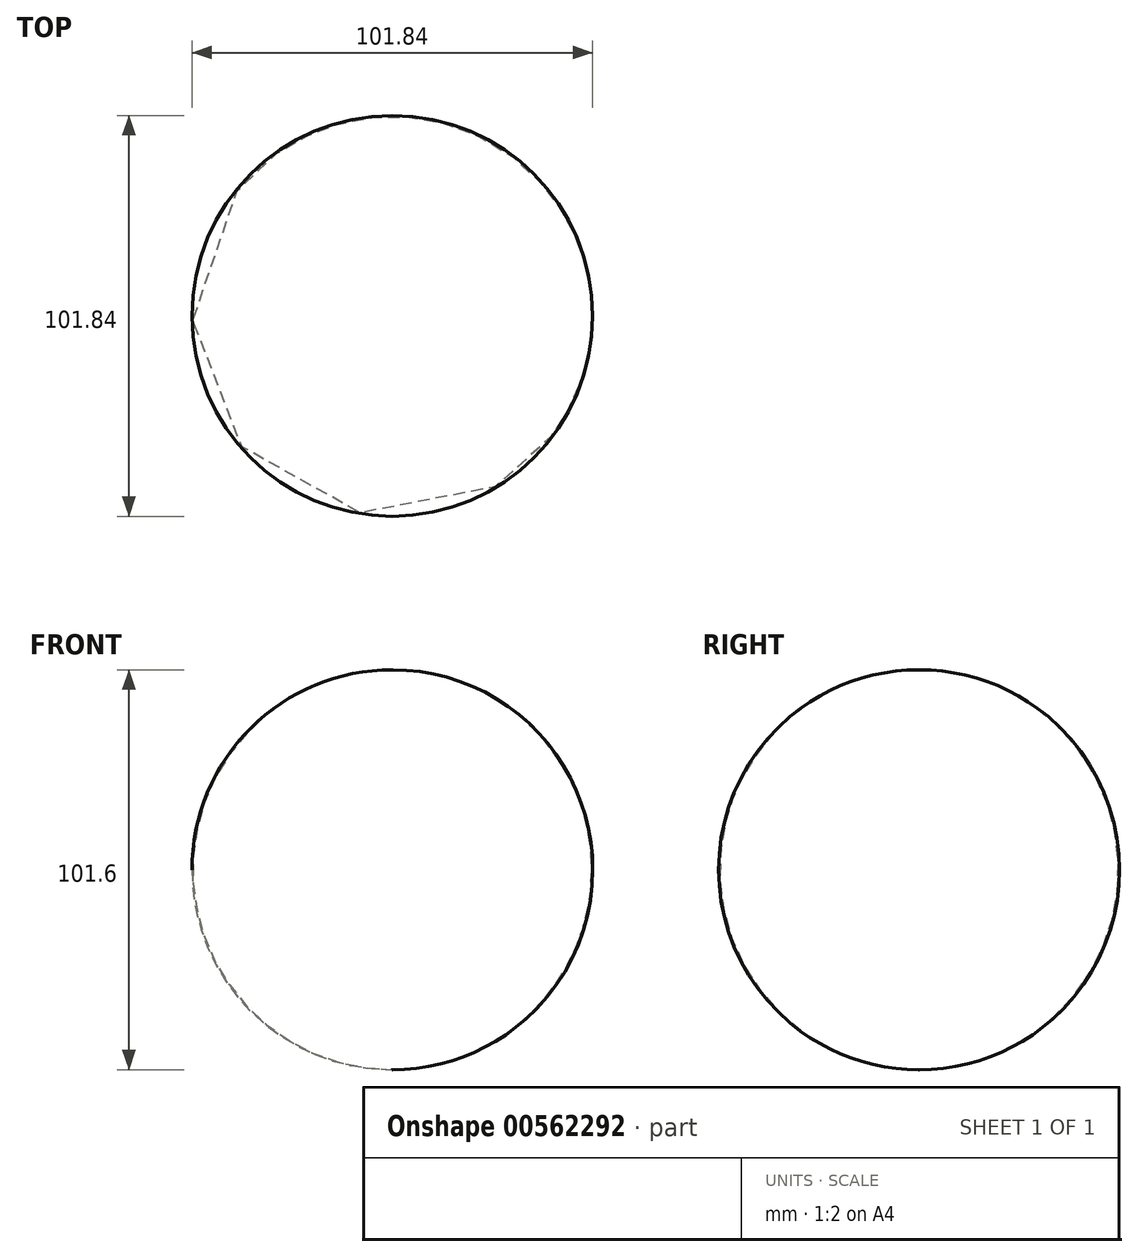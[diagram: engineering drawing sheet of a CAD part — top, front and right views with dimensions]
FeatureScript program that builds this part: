
annotation { "Feature Type Name" : "Feature", "Feature Type Description" : "" }
export const myFeature = defineFeature(function(context is Context, id is Id, definition is map)
    precondition{}
    {
        {
            var Q0;
            Q0=qCreatedBy(makeId("Front.planeOp"),FACE);
            var sketch = newSketch(context, id + "F0", { "sketchPlane" : qUnion([Q0])});
            skLineSegment(sketch, "E0", {"start": v(0, -48.96) * mm, "end": v(0, 52.64) * mm});
            skArc(sketch, "E1", {"start": v(0, -48.96) * mm, "mid": v(50.68, 1.84) * mm, "end": v(0, 52.64) * mm});
            skSolve(sketch);
        }
        {
            var Q0;
            Q0 = qSketchRegion(id + "F0", true);
            var Q1;
            Q1=sQuery(id+"F0.wireOp",EDGE,"E0");
            revolve(context, id + "F1", {"entities" : qUnion([Q0]), "axis" : qUnion([Q1]), "revolveType" : RevolveType.FULL});
        }
    });
